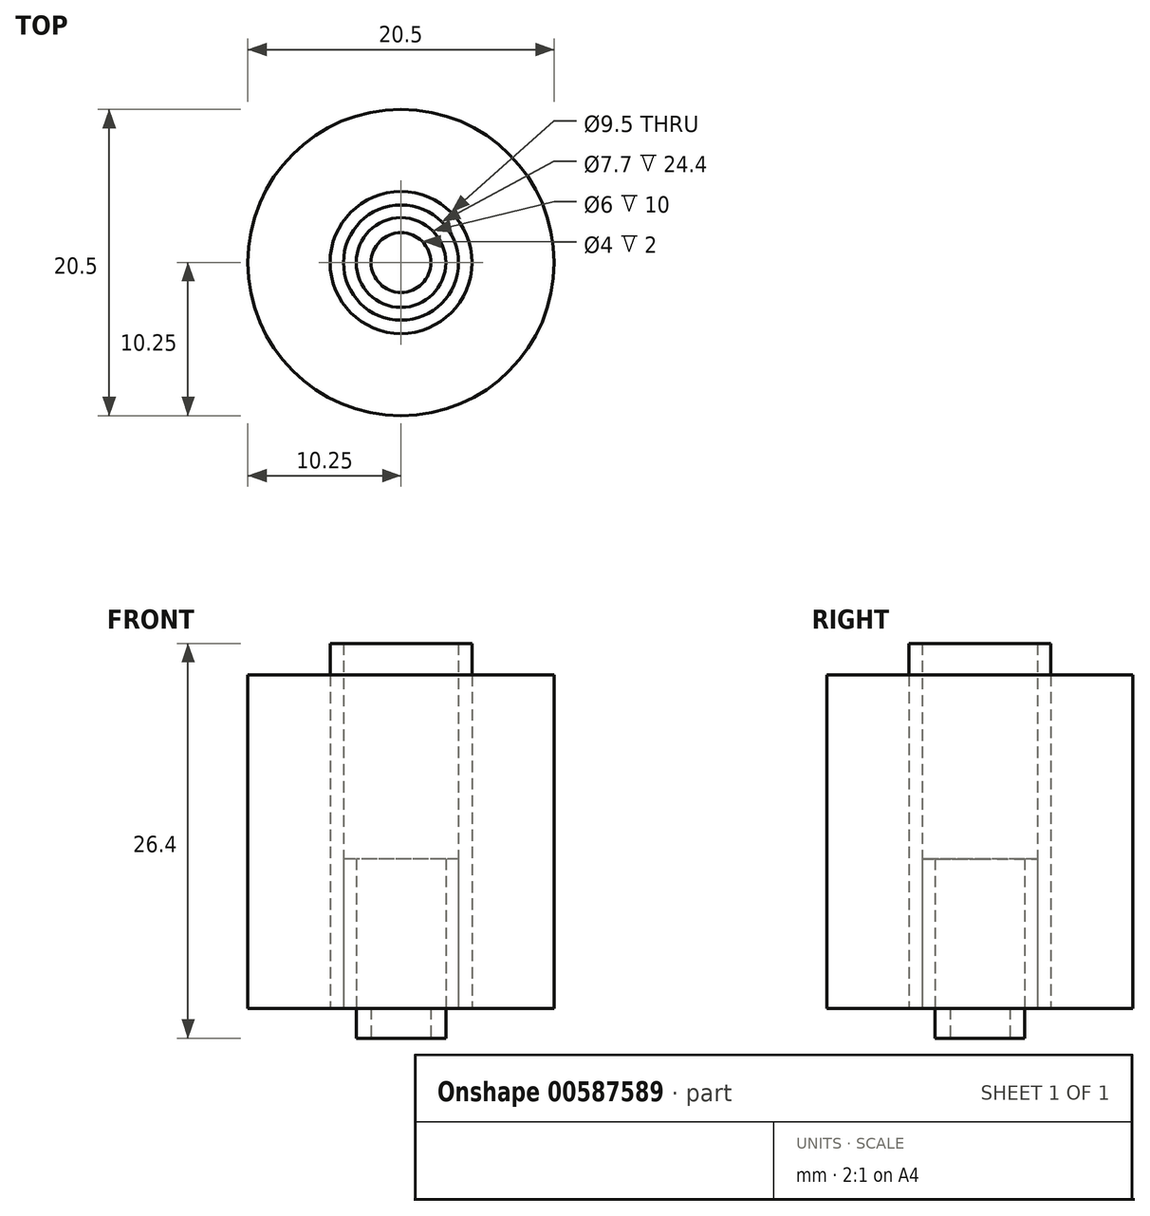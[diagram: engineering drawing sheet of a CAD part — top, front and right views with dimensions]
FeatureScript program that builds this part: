
annotation { "Feature Type Name" : "Feature", "Feature Type Description" : "" }
export const myFeature = defineFeature(function(context is Context, id is Id, definition is map)
    precondition{}
    {
        {
            var Q0;
            Q0=qCreatedBy(makeId("Top.planeOp"),FACE);
            var sketch = newSketch(context, id + "F0", { "sketchPlane" : qUnion([Q0])});
            skCircle(sketch, "E0", {"center": v(0, 0) * mm, "radius": 3 * mm});
            skCircle(sketch, "E1", {"center": v(0, 0) * mm, "radius": 2 * mm});
            skSolve(sketch);
        }
        {
            var Q0;
            Q0=makeQuery(id+"F0.imprint","IMPRINT",FACE,{"disambiguationData":[TD([[makeQuery(id+"F0.imprint","IMPRINT",EDGE,{"derivedFrom":sQuery(id+"F0.wireOp",EDGE,"E0")}),1.0]])]});
            extrude(context, id + "F1", {"entities" : qUnion([Q0]), "depth" : 2 * mm, "offsetDistance" : 25 * mm});
        }
        {
            var Q0;
            Q0=makeQuery(id+"F1.opExtrude","CAP_FACE",FACE,{"disambiguationData":[OSD([sQuery(id+"F0.wireOp",EDGE,"E0"),sQuery(id+"F0.wireOp",EDGE,"E1")])],"isStart":false});
            var sketch = newSketch(context, id + "F2", { "sketchPlane" : qUnion([Q0])});
            skCircle(sketch, "E2", {"center": v(0, 0) * mm, "radius": 10.25 * mm});
            skCircle(sketch, "E3", {"center": v(0, 0) * mm, "radius": 3 * mm});
            skCircle(sketch, "E4", {"center": v(0, 0) * mm, "radius": 2 * mm});
            skCircle(sketch, "E5", {"center": v(0, 0) * mm, "radius": 3.85 * mm});
            skCircle(sketch, "E6", {"center": v(0, 0) * mm, "radius": 4.75 * mm});
            skSolve(sketch);
        }
        {
            var Q0;
            Q0=makeQuery(id+"F2.imprint","IMPRINT",FACE,{"disambiguationData":[TD([[makeQuery(id+"F2.imprint","IMPRINT",EDGE,{"derivedFrom":sQuery(id+"F2.wireOp",EDGE,"E5")}),-1.0]])]});
            extrude(context, id + "F3", {"entities" : qUnion([Q0]), "depth" : 24.4 * mm, "offsetDistance" : 25 * mm});
        }
        {
            var Q0;
            Q0=makeQuery(id+"F2.imprint","IMPRINT",FACE,{"disambiguationData":[TD([[makeQuery(id+"F2.imprint","IMPRINT",EDGE,{"derivedFrom":sQuery(id+"F2.wireOp",EDGE,"E3")}),-1.0]])]});
            extrude(context, id + "F4", {"entities" : qUnion([Q0]), "depth" : 10 * mm, "offsetDistance" : 25 * mm});
        }
        {
            var Q0;
            Q0=makeQuery(id+"F2.imprint","IMPRINT",FACE,{"disambiguationData":[TD([[makeQuery(id+"F2.imprint","IMPRINT",EDGE,{"derivedFrom":sQuery(id+"F2.wireOp",EDGE,"E2")}),1.0]])]});
            extrude(context, id + "F5", {"entities" : qUnion([Q0]), "depth" : 22.3 * mm, "offsetDistance" : 25 * mm});
        }
    });
